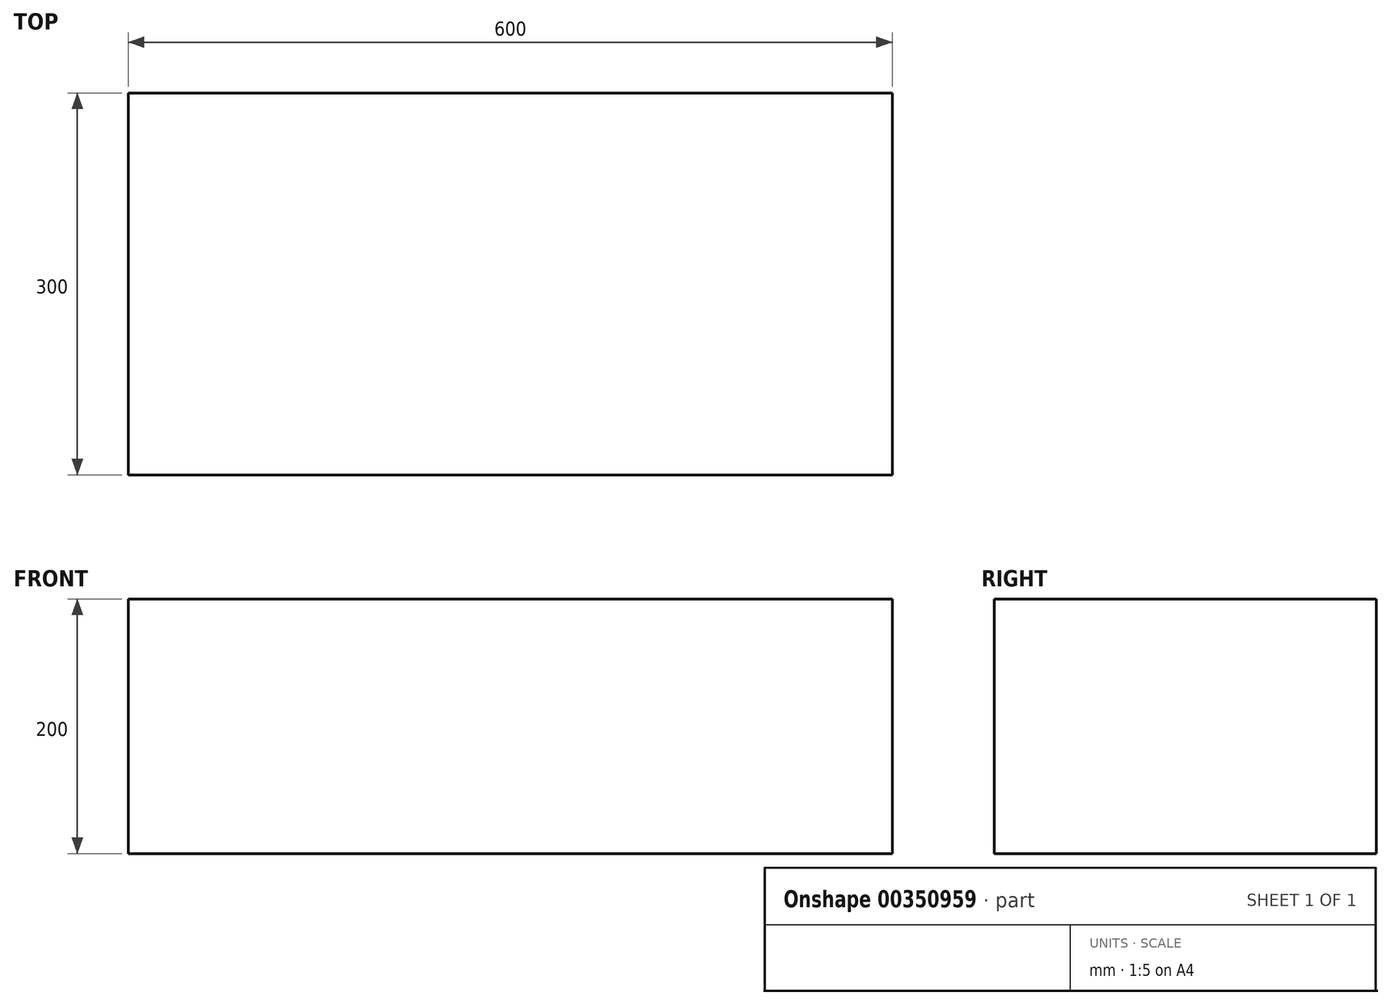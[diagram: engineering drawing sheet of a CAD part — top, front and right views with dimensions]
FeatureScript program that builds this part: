
annotation { "Feature Type Name" : "Feature", "Feature Type Description" : "" }
export const myFeature = defineFeature(function(context is Context, id is Id, definition is map)
    precondition{}
    {
        {
            var Q0;
            Q0=qCreatedBy(makeId("Front.planeOp"),FACE);
            var sketch = newSketch(context, id + "F0", { "sketchPlane" : qUnion([Q0])});
            skLineSegment(sketch, "E0.bottom", {"start": v(-300, 100) * mm, "end": v(300, 100) * mm});
            skLineSegment(sketch, "E0.top", {"start": v(-300, -100) * mm, "end": v(300, -100) * mm});
            skLineSegment(sketch, "E0.left", {"start": v(-300, 100) * mm, "end": v(-300, -100) * mm});
            skLineSegment(sketch, "E0.right", {"start": v(300, 100) * mm, "end": v(300, -100) * mm});
            skPoint(sketch, "E0.middle", {"position": v(0, 0) * mm});
            skSolve(sketch);
        }
        {
            var Q0;
            Q0 = qSketchRegion(id + "F0", true);
            extrude(context, id + "F1", {"entities" : qUnion([Q0]), "depth" : 300 * mm});
        }
    });
